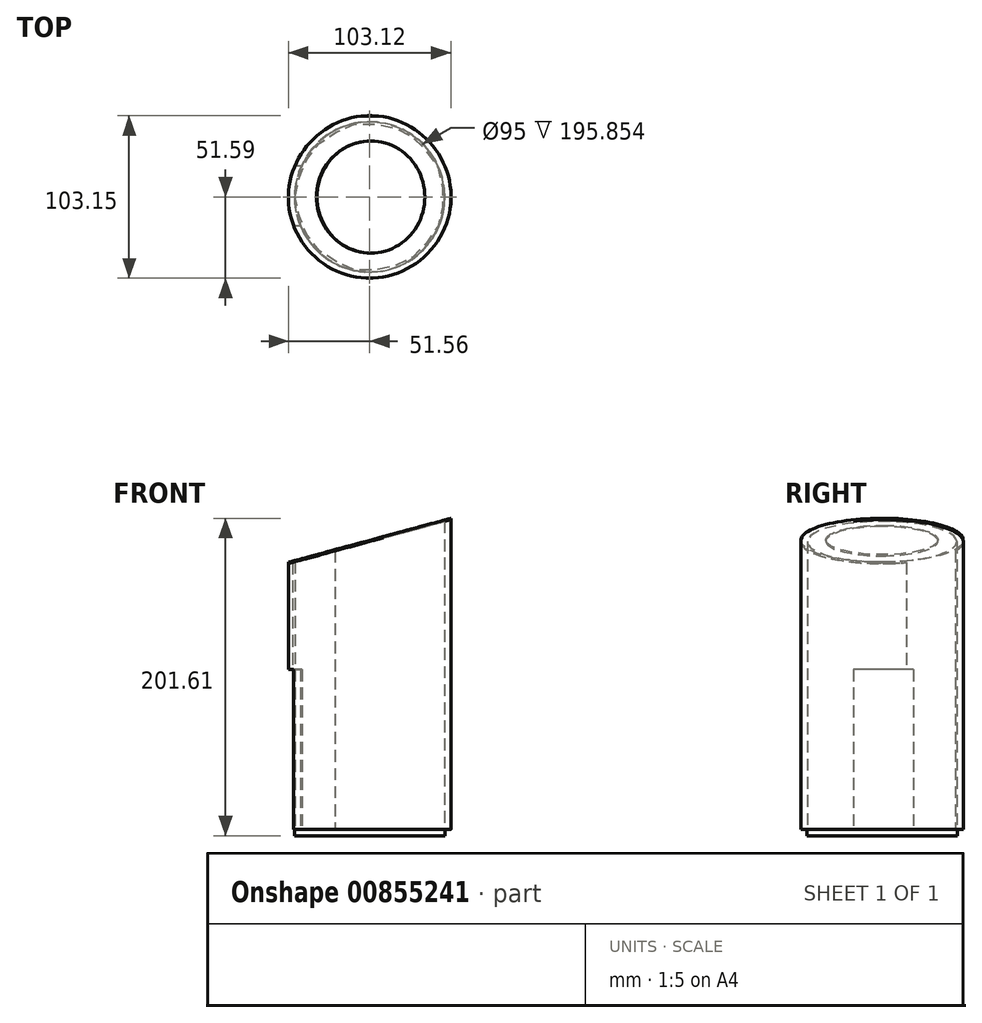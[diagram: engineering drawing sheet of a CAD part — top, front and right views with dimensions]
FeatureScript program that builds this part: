
annotation { "Feature Type Name" : "Feature", "Feature Type Description" : "" }
export const myFeature = defineFeature(function(context is Context, id is Id, definition is map)
    precondition{}
    {
        {
            var Q0;
            Q0=qCreatedBy(makeId("Top.planeOp"),FACE);
            var sketch = newSketch(context, id + "F0", { "sketchPlane" : qUnion([Q0])});
            skCircle(sketch, "E0", {"center": v(0, 0) * mm, "radius": 51.56 * mm});
            skCircle(sketch, "E1", {"center": v(0, 0) * mm, "radius": 47.5 * mm});
            skSolve(sketch);
        }
        {
            var Q0;
            Q0=qSketchRegion(id+"F0",true);
            extrude(context, id + "F1", {"entities" : qUnion([Q0]), "depth" : 196.85 * mm, "offsetDistance" : 25 * mm});
        }
        {
            var Q0;
            Q0=qCreatedBy(makeId("Front.planeOp"),FACE);
            var sketch = newSketch(context, id + "F2", { "sketchPlane" : qUnion([Q0])});
            skLineSegment(sketch, "E2", {"start": v(-56.99, 0) * mm, "end": v(-56.99, 168.91) * mm, "construction": true});
            skLineSegment(sketch, "E3", {"start": v(-51.54, 168.91) * mm, "end": v(53.58, 197.32) * mm});
            skLineSegment(sketch, "E4", {"start": v(53.58, 197.32) * mm, "end": v(-53.91, 197.32) * mm});
            skLineSegment(sketch, "E5", {"start": v(-53.91, 197.32) * mm, "end": v(-51.54, 168.91) * mm});
            skSolve(sketch);
        }
        {
            var Q0;
            Q0=qSketchRegion(id+"F2",true);
            extrude(context, id + "F3", {"entities" : qUnion([Q0]), "operationType" : NewBodyOperationType.REMOVE, "depth" : 61 * mm, "offsetDistance" : 25 * mm, "hasSecondDirection" : true, "secondDirectionOppositeDirection" : true, "secondDirectionDepth" : 74 * mm});
        }
        {
            var Q0;
            Q0=qCreatedBy(makeId("Right.planeOp"),FACE);
            var sketch = newSketch(context, id + "F4", { "sketchPlane" : qUnion([Q0])});
            skLineSegment(sketch, "E6.bottom", {"start": v(20.02, 101.6) * mm, "end": v(-18.08, 101.6) * mm});
            skLineSegment(sketch, "E6.top", {"start": v(20.02, 0) * mm, "end": v(-18.08, 0) * mm});
            skLineSegment(sketch, "E6.left", {"start": v(20.02, 101.6) * mm, "end": v(20.02, 0) * mm});
            skLineSegment(sketch, "E6.right", {"start": v(-18.08, 101.6) * mm, "end": v(-18.08, 0) * mm});
            skSolve(sketch);
        }
        {
            var Q0;
            Q0=qSketchRegion(id+"F4",true);
            extrude(context, id + "F5", {"entities" : qUnion([Q0]), "operationType" : NewBodyOperationType.REMOVE, "oppositeDirection" : true, "depth" : 61 * mm, "offsetDistance" : 25 * mm});
        }
        {
            var Q0;
            Q0=qCreatedBy(makeId("Front.planeOp"),FACE);
            cPlane(context, id + "F6", {"entities" : qUnion([Q0]), "cplaneType" : CPlaneType.OFFSET, "offset" : 51.59 * mm, "width" : 150 * mm, "height" : 150 * mm});
        }
        {
            var Q0;
            Q0=qCreatedBy(id+"F6.planeOp",FACE);
            var sketch = newSketch(context, id + "F7", { "sketchPlane" : qUnion([Q0])});
            skLineSegment(sketch, "E7", {"start": v(-51.56, 168.9) * mm, "end": v(51.56, 196.78) * mm});
            skLineSegment(sketch, "E8", {"start": v(51.56, 196.78) * mm, "end": v(51.56, 197.61) * mm});
            skLineSegment(sketch, "E9", {"start": v(51.56, 197.61) * mm, "end": v(-51.56, 169.73) * mm});
            skLineSegment(sketch, "E10", {"start": v(-51.56, 169.73) * mm, "end": v(-51.56, 168.9) * mm});
            skSolve(sketch);
        }
        {
            var Q0;
            Q0=qSketchRegion(id+"F7",true);
            extrude(context, id + "F8", {"entities" : qUnion([Q0]), "operationType" : NewBodyOperationType.ADD, "oppositeDirection" : true, "depth" : 103.1 * mm, "offsetDistance" : 25 * mm});
        }
        {
            var Q0;
            Q0=qCreatedBy(makeId("Top.planeOp"),FACE);
            var sketch = newSketch(context, id + "F9", { "sketchPlane" : qUnion([Q0])});
            skArc(sketch, "E11", {"start": v(0, 51.9) * mm, "mid": v(-36.37, 36.4) * mm, "end": v(-51.78, 0) * mm});
            skArc(sketch, "E12", {"start": v(51.78, 0) * mm, "mid": v(36.45, 36.49) * mm, "end": v(0, 51.9) * mm});
            skArc(sketch, "E13", {"start": v(0, -51.65) * mm, "mid": v(36.4, -36.36) * mm, "end": v(51.78, 0) * mm});
            skArc(sketch, "E14", {"start": v(-51.78, 0) * mm, "mid": v(-36.49, -36.45) * mm, "end": v(0, -51.65) * mm});
            skLineSegment(sketch, "E15", {"start": v(-51.78, 0) * mm, "end": v(-55.26, 0) * mm});
            skLineSegment(sketch, "E16", {"start": v(-55.26, 0) * mm, "end": v(-55.26, 55.12) * mm});
            skLineSegment(sketch, "E17", {"start": v(-55.26, 55.12) * mm, "end": v(54.05, 51.9) * mm});
            skLineSegment(sketch, "E18", {"start": v(54.05, 51.9) * mm, "end": v(54.05, -56.1) * mm});
            skLineSegment(sketch, "E19", {"start": v(54.05, -56.1) * mm, "end": v(-55.26, -56.1) * mm});
            skLineSegment(sketch, "E20", {"start": v(-55.26, -56.1) * mm, "end": v(-55.26, 0) * mm});
            skSolve(sketch);
        }
        {
            var Q0;
            Q0=makeQuery(id+"F9.imprint","IMPRINT",FACE,{"disambiguationData":[TD([[makeQuery(id+"F9.imprint","IMPRINT",EDGE,{"derivedFrom":sQuery(id+"F9.wireOp",EDGE,"E11")}),-1.0]])]});
            extrude(context, id + "F10", {"entities" : qUnion([Q0]), "operationType" : NewBodyOperationType.REMOVE, "depth" : 222 * mm, "offsetDistance" : 25 * mm});
        }
        {
            var Q0;
            Q0=makeQuery(id+"F8.opExtrude","SWEPT_FACE",FACE,{"disambiguationData":[OSD([sQuery(id+"F7.wireOp",EDGE,"E9")])]});
            cPlane(context, id + "F11", {"entities" : qUnion([Q0]), "cplaneType" : CPlaneType.OFFSET, "offset" : 0.3 * mm, "width" : 150 * mm, "height" : 150 * mm});
        }
        {
            var Q0;
            Q0=qCreatedBy(id+"F11.planeOp",FACE);
            var sketch = newSketch(context, id + "F12", { "sketchPlane" : qUnion([Q0])});
            skCircle(sketch, "E21", {"center": v(48.6, 0) * mm, "radius": 35.6 * mm});
            skSolve(sketch);
        }
        {
            var Q0;
            Q0=qSketchRegion(id+"F12",true);
            extrude(context, id + "F13", {"entities" : qUnion([Q0]), "operationType" : NewBodyOperationType.REMOVE, "oppositeDirection" : true, "depth" : 6.3 * mm, "offsetDistance" : 25 * mm});
        }
        {
            var Q0;
            Q0=qCreatedBy(makeId("Top.planeOp"),FACE);
            var sketch = newSketch(context, id + "F14", { "sketchPlane" : qUnion([Q0])});
            skCircle(sketch, "E22", {"center": v(0, 0) * mm, "radius": 47.76 * mm});
            skSolve(sketch);
        }
        {
            var Q0;
            Q0 = qSketchRegion(id + "F14", true);
            extrude(context, id + "F15", {"entities" : qUnion([Q0]), "operationType" : NewBodyOperationType.ADD, "oppositeDirection" : true, "depth" : 4 * mm, "offsetDistance" : 25 * mm});
        }
    });
